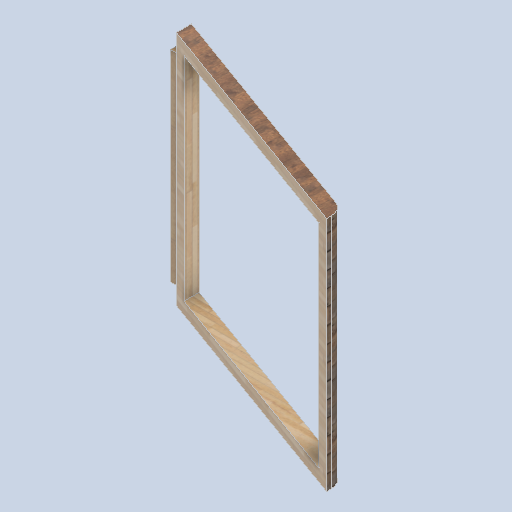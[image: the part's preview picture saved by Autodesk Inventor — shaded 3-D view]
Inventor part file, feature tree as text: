
AUTODESK INVENTOR PART (.ipt)
format: ipt  version: 2024.2 (Build 282272000, 272)  size: 163,328 bytes
history: native  units: in
note: dims shown in document units (in); Inventor stores cm internally (conversion verified against a paired STEP export)
features: sketch x5, other x3, plane x1
ambient origin geometry x8: Origin, YZ Plane, XZ Plane, XY Plane, X Axis, Y Axis, Z Axis, Center Point
bodies: Solid1 (feature_tree)
feature tree (9):
  other  "side_curve_frame_01.ipt"
  other  "Solid1::side_curve_frame_01.ipt"
  other  "TaggingFeature1"
  sketch  "Sketch1"  dims[d0=0.3937in]
  sketch  "Sketch2"
  sketch  "Sketch3"
  sketch  "Sketch4"
  sketch  "Sketch5"
  plane  "Work Plane1"
